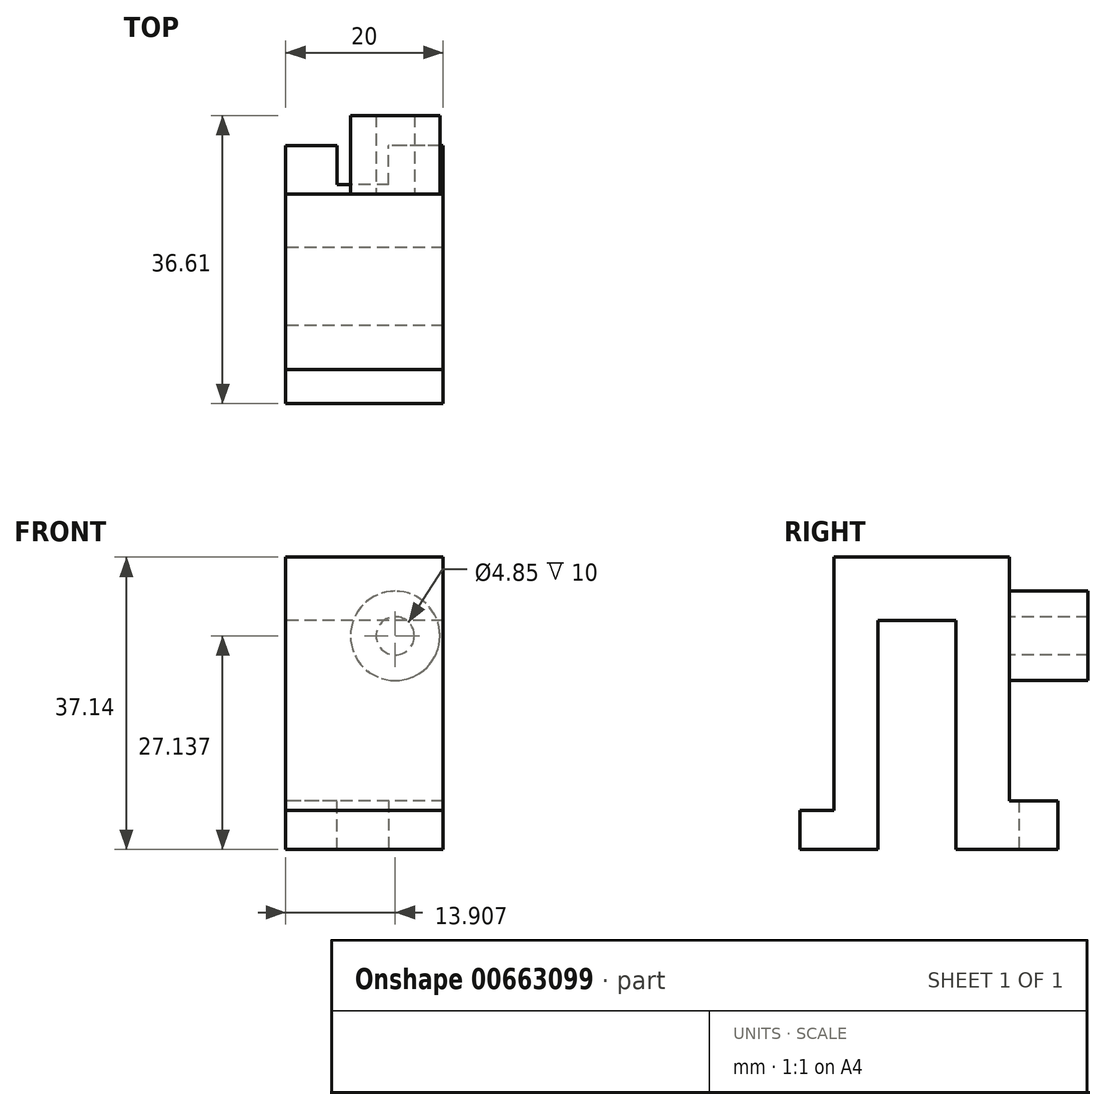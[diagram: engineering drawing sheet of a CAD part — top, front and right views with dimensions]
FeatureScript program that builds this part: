
annotation { "Feature Type Name" : "Feature", "Feature Type Description" : "" }
export const myFeature = defineFeature(function(context is Context, id is Id, definition is map)
    precondition{}
    {
        {
            var Q0;
            Q0=qCreatedBy(makeId("Right.planeOp"),FACE);
            var sketch = newSketch(context, id + "F0", { "sketchPlane" : qUnion([Q0])});
            skLineSegment(sketch, "E0", {"start": v(-50.6, -13.3) * mm, "end": v(-50.6, -18.26) * mm});
            skLineSegment(sketch, "E1", {"start": v(-50.6, -18.26) * mm, "end": v(-40.7, -18.26) * mm});
            skLineSegment(sketch, "E2", {"start": v(-40.7, -18.26) * mm, "end": v(-40.7, 10.83) * mm});
            skLineSegment(sketch, "E3", {"start": v(-40.7, 10.83) * mm, "end": v(-30.79, 10.83) * mm});
            skLineSegment(sketch, "E4", {"start": v(-30.79, 10.83) * mm, "end": v(-30.79, -18.26) * mm});
            skLineSegment(sketch, "E5", {"start": v(-30.79, -18.26) * mm, "end": v(-17.8, -18.26) * mm});
            skLineSegment(sketch, "E6", {"start": v(-17.8, -18.26) * mm, "end": v(-17.8, -12.07) * mm});
            skLineSegment(sketch, "E7", {"start": v(-17.8, -12.07) * mm, "end": v(-23.98, -12.07) * mm});
            skLineSegment(sketch, "E8", {"start": v(-23.98, -12.07) * mm, "end": v(-23.98, 18.88) * mm});
            skLineSegment(sketch, "E9", {"start": v(-23.98, 18.88) * mm, "end": v(-46.26, 18.88) * mm});
            skLineSegment(sketch, "E10", {"start": v(-46.26, 18.88) * mm, "end": v(-46.26, -13.3) * mm});
            skLineSegment(sketch, "E11", {"start": v(-46.26, -13.3) * mm, "end": v(-50.6, -13.3) * mm});
            skSolve(sketch);
        }
        {
            var Q0;
            Q0=makeQuery(id+"F0.imprint","IMPRINT",FACE,{"disambiguationData":[TD([[makeQuery(id+"F0.imprint","IMPRINT",EDGE,{"derivedFrom":sQuery(id+"F0.wireOp",EDGE,"E0")}),1.0]])]});
            extrude(context, id + "F1", {"entities" : qUnion([Q0]), "depth" : 20 * mm, "offsetDistance" : 25 * mm});
        }
        {
            var Q0;
            Q0=makeQuery(id+"F1.opExtrude","SWEPT_FACE",FACE,{"disambiguationData":[OSD([sQuery(id+"F0.wireOp",EDGE,"E6")])]});
            var sketch = newSketch(context, id + "F2", { "sketchPlane" : qUnion([Q0])});
            skLineSegment(sketch, "E12", {"start": v(-13.08, -12.07) * mm, "end": v(-13.08, -18.26) * mm});
            skLineSegment(sketch, "E13", {"start": v(-13.08, -18.26) * mm, "end": v(-6.53, -18.26) * mm});
            skLineSegment(sketch, "E14", {"start": v(-6.53, -18.26) * mm, "end": v(-6.53, -12.07) * mm});
            skLineSegment(sketch, "E15", {"start": v(-6.53, -12.07) * mm, "end": v(-13.08, -12.07) * mm});
            skSolve(sketch);
        }
        {
            var Q0;
            Q0=makeQuery(id+"F2.imprint","IMPRINT",FACE,{"disambiguationData":[TD([[makeQuery(id+"F2.imprint","IMPRINT",EDGE,{"derivedFrom":sQuery(id+"F2.wireOp",EDGE,"E12")}),1.0]])]});
            extrude(context, id + "F3", {"entities" : qUnion([Q0]), "operationType" : NewBodyOperationType.REMOVE, "oppositeDirection" : true, "depth" : 5 * mm, "offsetDistance" : 25 * mm});
        }
        {
            var Q0;
            Q0=makeQuery(id+"F1.opExtrude","SWEPT_FACE",FACE,{"disambiguationData":[OSD([sQuery(id+"F0.wireOp",EDGE,"E8")])]});
            var sketch = newSketch(context, id + "F4", { "sketchPlane" : qUnion([Q0])});
            skCircle(sketch, "E16", {"center": v(-13.9, 8.88) * mm, "radius": 5.68 * mm});
            skCircle(sketch, "E17", {"center": v(-13.9, 8.88) * mm, "radius": 2.42 * mm});
            skSolve(sketch);
        }
        {
            var Q0;
            Q0=makeQuery(id+"F4.imprint","IMPRINT",FACE,{"disambiguationData":[TD([[makeQuery(id+"F4.imprint","IMPRINT",EDGE,{"derivedFrom":sQuery(id+"F4.wireOp",EDGE,"E16")}),1.0]])]});
            extrude(context, id + "F5", {"entities" : qUnion([Q0]), "operationType" : NewBodyOperationType.ADD, "depth" : 10 * mm, "offsetDistance" : 25 * mm});
        }
    });
